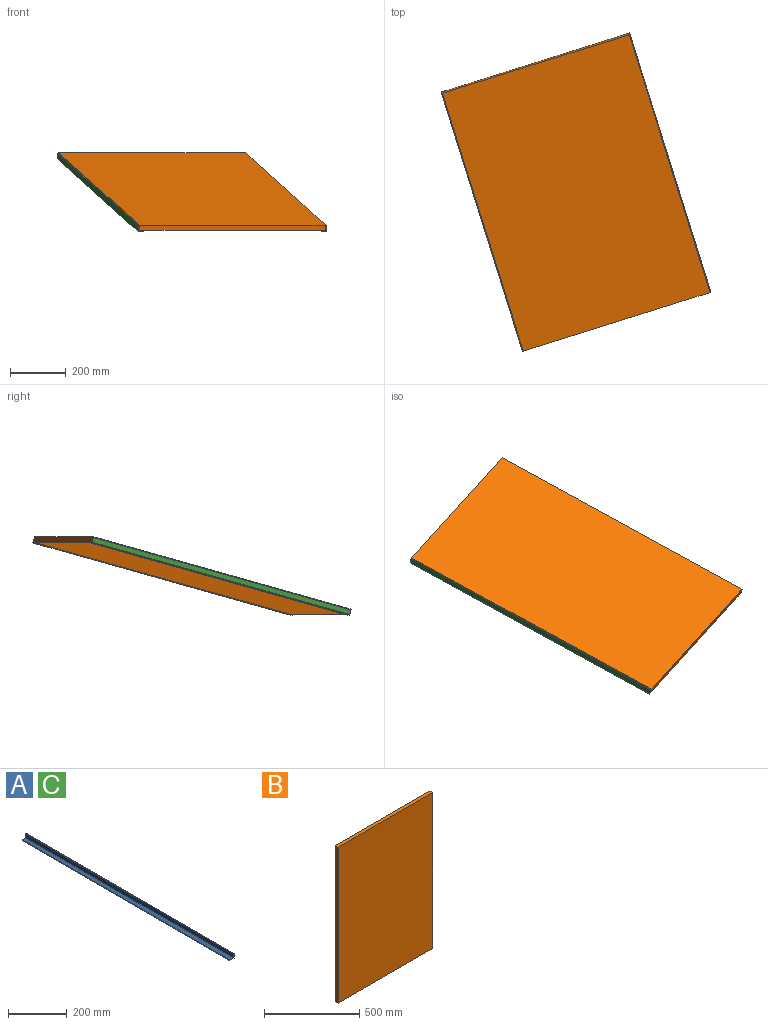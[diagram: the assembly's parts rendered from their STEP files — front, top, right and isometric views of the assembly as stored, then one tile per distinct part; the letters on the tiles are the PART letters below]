
ASSEMBLY  parts=3 mates=6
PART A: 8 faces, bbox 20x1000x20 mm
  f0: plane 1000x17mm, normal (0,0,1), area 17000mm2, adj f1,f5,f6,f7
  f1: plane 1000x3mm, normal (-1,0,0), area 3000mm2, adj f0,f2,f6,f7
  f2: plane 1000x20mm, normal (0,0,-1), area 20000mm2, adj f1,f3,f6,f7
  f3: plane 1000x20mm, normal (1,0,0), area 20000mm2, adj f2,f4,f6,f7
  f4: plane 1000x3mm, normal (0,0,1), area 3000mm2, adj f3,f5,f6,f7
  f5: plane 1000x17mm, normal (-1,0,0), area 17000mm2, adj f0,f4,f6,f7
  f6: plane 20x20mm, normal (0,-1,0), area 111mm2, adj f0,f1,f2,f3,f4,f5
  f7: plane 20x20mm, normal (0,1,0), area 111mm2, adj f0,f1,f2,f3,f4,f5
PART B: 6 faces, bbox 700x20x1000 mm
  f0: plane 1000x20mm, normal (-1,0,0), area 20000mm2, adj f1,f3,f4,f5
  f1: plane 700x20mm, normal (0,0,-1), area 14000mm2, adj f0,f2,f4,f5
  f2: plane 1000x20mm, normal (1,0,0), area 20000mm2, adj f1,f3,f4,f5
  f3: plane 700x20mm, normal (0,0,1), area 14000mm2, adj f0,f2,f4,f5
  f4: plane 1000x700mm, normal (0,-1,0), area 700000mm2, adj f0,f1,f2,f3
  f5: plane 1000x700mm, normal (0,1,0), area 700000mm2, adj f0,f1,f2,f3
PART C: same geometry as A
PLACE A rot(axis=(0.65,0.1,0.75),22.9deg) t=(-780.88,429.37,390.89)mm
PLACE B rot(axis=(0.98,0.15,0.12),106deg) t=(-952.28,-136.8,283.7)mm
PLACE C rot(axis=(-0.02,0.96,0.27),94.5deg) t=(-1433.88,219.11,410.21)mm
MATE planar A.f6 <-> C.f6  axis (0.29,-0.92,-0.26) through (-483.42,-490.46,134.97)mm
MATE planar B.f0 <-> C.f0  axis (-0.95,-0.3,0) through (-1287,-239.09,274.04)mm
MATE planar B.f1 <-> A.f7  axis (-0.29,0.92,0.26) through (-1097.61,326.49,403.45)mm
MATE planar A.f0 <-> B.f4  axis (0.08,-0.25,0.97) through (-627.98,-29.64,264.38)mm
MATE planar B.f2 <-> A.f5  axis (0.95,0.3,0) through (-619.1,-29.57,274.04)mm
MATE planar A.f2 <-> C.f3  axis (-0.08,0.25,-0.97) through (-626.78,-28.45,261.48)mm
